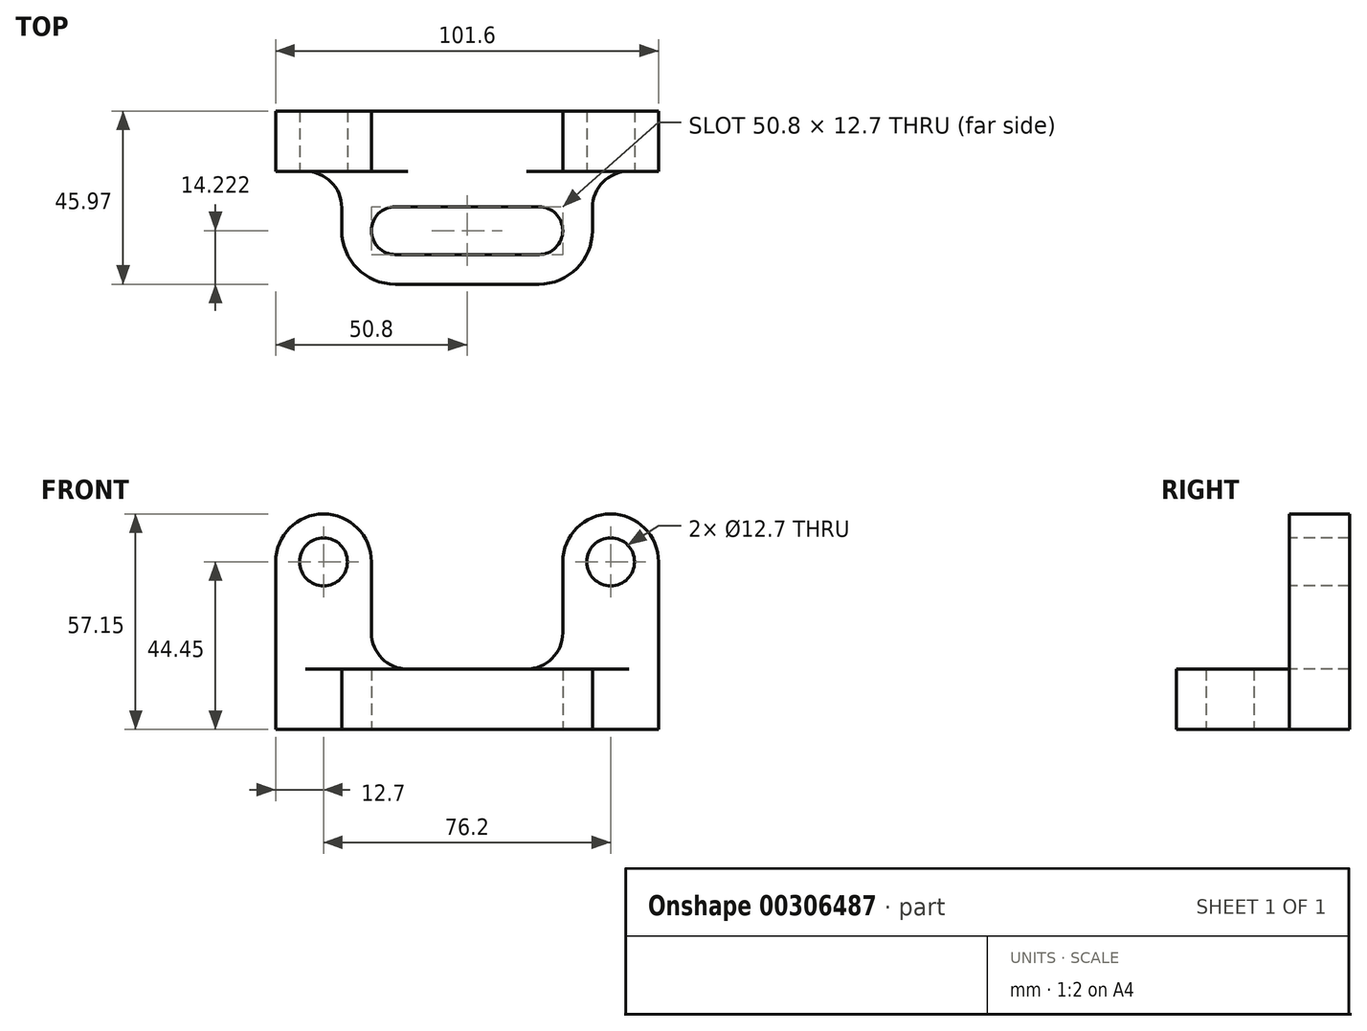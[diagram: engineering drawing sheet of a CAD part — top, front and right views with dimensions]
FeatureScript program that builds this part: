
annotation { "Feature Type Name" : "Feature", "Feature Type Description" : "" }
export const myFeature = defineFeature(function(context is Context, id is Id, definition is map)
    precondition{}
    {
        {
            var Q0;
            Q0=qCreatedBy(makeId("Front.planeOp"),FACE);
            var sketch = newSketch(context, id + "F0", { "sketchPlane" : qUnion([Q0])});
            skCircle(sketch, "E0", {"center": v(-38.1, 44.45) * mm, "radius": 6.35 * mm});
            skCircle(sketch, "E1.MirrorC", {"center": v(38.1, 44.45) * mm, "radius": 6.35 * mm});
            skArc(sketch, "E2", {"start": v(-50.8, 44.45) * mm, "mid": v(-38.1, 57.15) * mm, "end": v(-25.4, 44.45) * mm});
            skArc(sketch, "E3.MirrorCS", {"start": v(50.8, 44.45) * mm, "mid": v(38.1, 57.15) * mm, "end": v(25.4, 44.45) * mm});
            skLineSegment(sketch, "E4", {"start": v(-50.8, 44.45) * mm, "end": v(-50.8, 0) * mm});
            skLineSegment(sketch, "E5", {"start": v(-50.8, 0) * mm, "end": v(50.8, 0) * mm});
            skLineSegment(sketch, "E6", {"start": v(50.8, 0) * mm, "end": v(50.8, 44.45) * mm});
            skLineSegment(sketch, "E7", {"start": v(-15.75, 16) * mm, "end": v(15.75, 16) * mm});
            skLineSegment(sketch, "E8", {"start": v(-25.4, 44.45) * mm, "end": v(-25.4, 25.65) * mm});
            skPoint(sketch, "E9.visualSharp", {"position": v(-25.4, 16) * mm});
            skArc(sketch, "E9.filletArc", {"start": v(-25.4, 25.65) * mm, "mid": v(-22.57, 18.83) * mm, "end": v(-15.75, 16) * mm});
            skLineSegment(sketch, "E10", {"start": v(25.4, 44.45) * mm, "end": v(25.4, 25.65) * mm});
            skPoint(sketch, "E11.visualSharp", {"position": v(25.4, 16) * mm});
            skArc(sketch, "E11.filletArc", {"start": v(15.75, 16) * mm, "mid": v(22.57, 18.83) * mm, "end": v(25.4, 25.65) * mm});
            skSolve(sketch);
        }
        {
            var Q0;
            Q0 = qSketchRegion(id + "F0", true);
            extrude(context, id + "F1", {"entities" : qUnion([Q0]), "oppositeDirection" : true, "depth" : 16 * mm});
        }
        {
            var Q0;
            Q0=qCreatedBy(makeId("Top.planeOp"),FACE);
            var sketch = newSketch(context, id + "F2", { "sketchPlane" : qUnion([Q0])});
            skLineSegment(sketch, "E12.bottom", {"start": v(-33.27, 0) * mm, "end": v(33.27, 0) * mm});
            skLineSegment(sketch, "E12.top", {"start": v(-19.05, -29.97) * mm, "end": v(19.05, -29.97) * mm});
            skLineSegment(sketch, "E12.left", {"start": v(-33.27, -9.65) * mm, "end": v(-33.27, -15.75) * mm});
            skLineSegment(sketch, "E12.right", {"start": v(33.27, -9.65) * mm, "end": v(33.27, -15.75) * mm});
            skPoint(sketch, "E13.visualSharp", {"position": v(-33.27, -29.97) * mm});
            skArc(sketch, "E13.filletArc", {"start": v(-33.27, -15.75) * mm, "mid": v(-29.1, -25.8) * mm, "end": v(-19.05, -29.97) * mm});
            skPoint(sketch, "E14.visualSharp", {"position": v(33.27, -29.97) * mm});
            skArc(sketch, "E14.filletArc", {"start": v(19.05, -29.97) * mm, "mid": v(29.1, -25.8) * mm, "end": v(33.27, -15.75) * mm});
            skLineSegment(sketch, "E15", {"start": v(-19.05, -9.4) * mm, "end": v(19.05, -9.4) * mm});
            skLineSegment(sketch, "E16", {"start": v(19.05, -9.4) * mm, "end": v(-19.05, -9.4) * mm});
            skLineSegment(sketch, "E17", {"start": v(-19.05, -22.1) * mm, "end": v(19.05, -22.1) * mm});
            skArc(sketch, "E18", {"start": v(-19.05, -9.4) * mm, "mid": v(-25.4, -15.75) * mm, "end": v(-19.05, -22.1) * mm});
            skArc(sketch, "E19", {"start": v(19.05, -22.1) * mm, "mid": v(25.4, -15.75) * mm, "end": v(19.05, -9.4) * mm});
            skPoint(sketch, "E20", {"position": v(0, -9.4) * mm});
            skLineSegment(sketch, "E21", {"start": v(-42.93, 0) * mm, "end": v(-60.48, 0) * mm, "construction": true});
            skLineSegment(sketch, "E22", {"start": v(42.93, 0) * mm, "end": v(70.53, 0) * mm, "construction": true});
            skPoint(sketch, "E23.visualSharp", {"position": v(-33.27, 0) * mm});
            skArc(sketch, "E23.filletArc", {"start": v(-33.27, -9.65) * mm, "mid": v(-36.1, -2.83) * mm, "end": v(-42.93, 0) * mm});
            skPoint(sketch, "E24.visualSharp", {"position": v(33.27, 0) * mm});
            skArc(sketch, "E24.filletArc", {"start": v(42.93, 0) * mm, "mid": v(36.1, -2.83) * mm, "end": v(33.27, -9.65) * mm});
            skLineSegment(sketch, "E25", {"start": v(-42.93, 0) * mm, "end": v(42.93, 0) * mm});
            skSolve(sketch);
        }
        {
            var Q0;
            Q0 = qSketchRegion(id + "F2", true);
            extrude(context, id + "F3", {"entities" : qUnion([Q0]), "operationType" : NewBodyOperationType.ADD, "depth" : 16 * mm});
        }
    });
